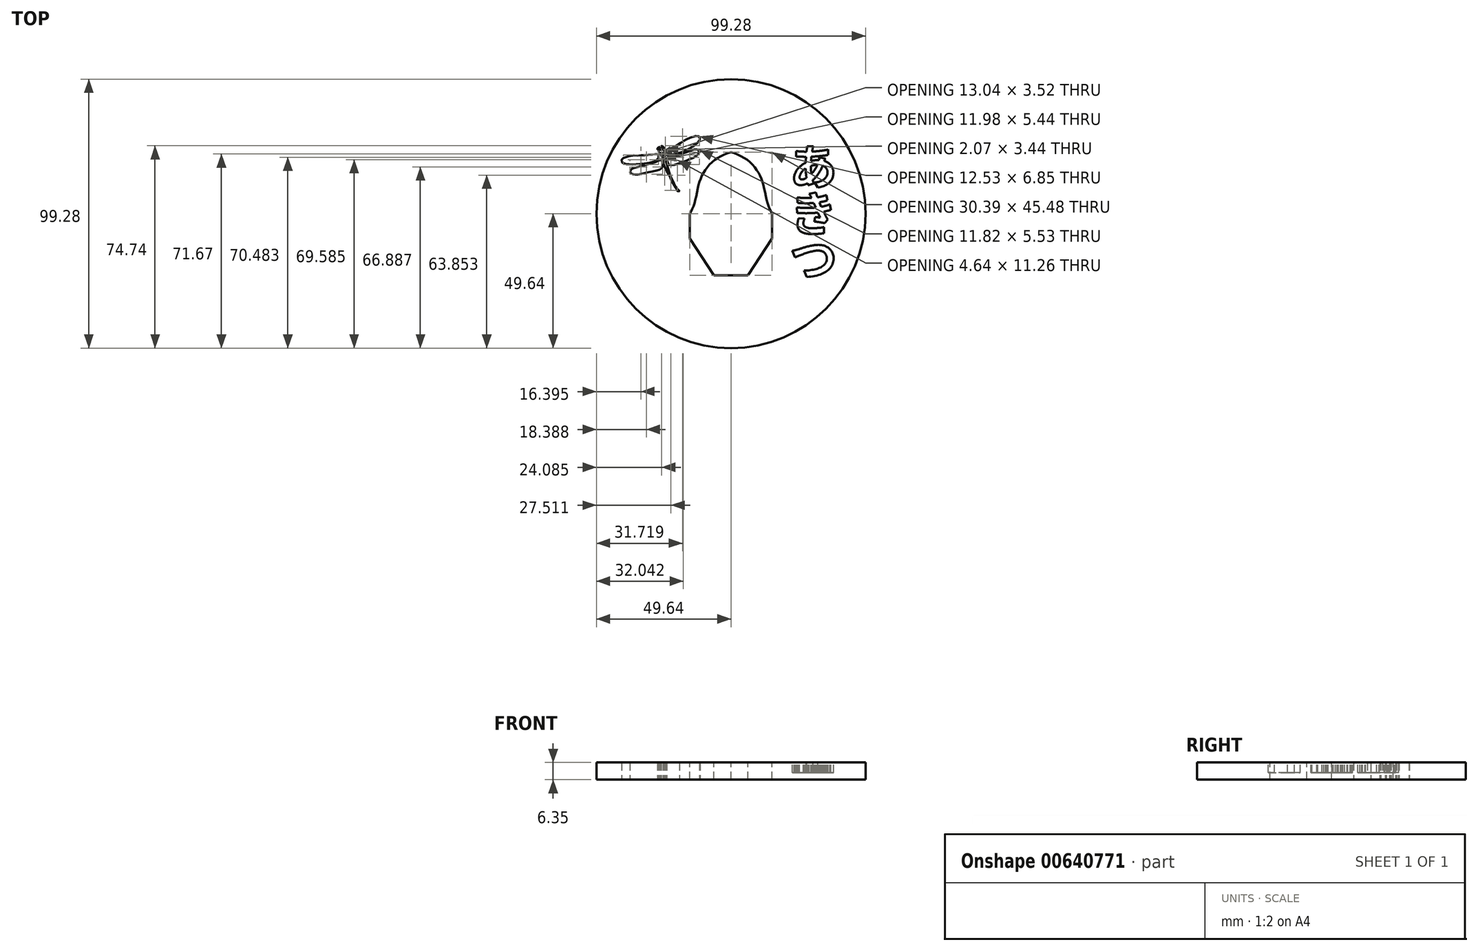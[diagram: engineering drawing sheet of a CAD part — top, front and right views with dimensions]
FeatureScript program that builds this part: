
annotation { "Feature Type Name" : "Feature", "Feature Type Description" : "" }
export const myFeature = defineFeature(function(context is Context, id is Id, definition is map)
    precondition{}
    {
        {
            var Q0;
            Q0=qCreatedBy(makeId("Top.planeOp"),FACE);
            var sketch = newSketch(context, id + "F0", { "sketchPlane" : qUnion([Q0])});
            skLineSegment(sketch, "E0.top", {"start": v(6.27, -22.74) * mm, "end": v(-6.27, -22.74) * mm});
            skLineSegment(sketch, "E0.left", {"start": v(15.2, 0) * mm, "end": v(15.2, -9.14) * mm});
            skLineSegment(sketch, "E0.right", {"start": v(-15.2, 0) * mm, "end": v(-15.2, -9.14) * mm});
            skPoint(sketch, "E0.middle", {"position": v(0, 0) * mm});
            skLineSegment(sketch, "E1", {"start": v(-15.2, -9.14) * mm, "end": v(-6.27, -22.74) * mm});
            skFitSpline(sketch, "E2", {"points": [v(0, 22.74) * mm, v(-5.84, 19.98) * mm, v(-9.88, 15.51) * mm, v(-12, 10.41) * mm, v(-13.5, 3.83) * mm, v(-15.2, 0) * mm], "startDerivative": vector(-29.13, -10.82) * mm, "endDerivative": vector(-10.85, -20.26) * mm});
            skFitSpline(sketch, "E3.MirrorCS", {"points": [v(0, 22.74) * mm, v(5.84, 19.98) * mm, v(9.88, 15.51) * mm, v(12, 10.41) * mm, v(13.5, 3.83) * mm, v(15.2, 0) * mm], "startDerivative": vector(29.13, -10.82) * mm, "endDerivative": vector(10.85, -20.26) * mm});
            skLineSegment(sketch, "E4.MirrorCS", {"start": v(15.2, -9.14) * mm, "end": v(6.27, -22.74) * mm});
            skPoint(sketch, "E5.orphan", {"position": v(-15.2, 22.74) * mm});
            skPoint(sketch, "E6.orphan", {"position": v(15.2, 22.74) * mm});
            skPoint(sketch, "E7.orphan", {"position": v(15.2, -22.74) * mm});
            skPoint(sketch, "E8.orphan", {"position": v(-15.2, -22.74) * mm});
            skCircle(sketch, "E9", {"center": v(0, 0) * mm, "radius": 49.64 * mm});
            skSolve(sketch);
        }
        {
            var Q0;
            Q0 = qSketchRegion(id + "F0", true);
            extrude(context, id + "F1", {"entities" : qUnion([Q0]), "oppositeDirection" : true, "depth" : 6.35 * mm, "offsetDistance" : 25.4 * mm});
        }
        {
            var Q0;
            Q0=qCreatedBy(makeId("Top.planeOp"),FACE);
            var sketch = newSketch(context, id + "F2", { "sketchPlane" : qUnion([Q0])});
            skEllipse(sketch, "E10", {"center": v(-25.17, 24.54) * mm, "majorRadius": 0.65 * mm, "minorRadius": 0.24 * mm, "majorAxis": v(0.78, -0.62)});
            skEllipse(sketch, "E11", {"center": v(-26.7, 24.17) * mm, "majorRadius": 0.6 * mm, "minorRadius": 0.27 * mm, "majorAxis": v(0.7, 0.72)});
            skFitSpline(sketch, "E12", {"points": [v(-24.63, 23.55) * mm, v(-24.92, 23.68) * mm, v(-25.48, 23.76) * mm, v(-26.25, 23.56) * mm, v(-26.58, 23.21) * mm, v(-26.45, 22.59) * mm, v(-26.17, 22.45) * mm, v(-25.86, 22.12) * mm, v(-25.2, 20.37) * mm, v(-24.92, 20.22) * mm, v(-24.5, 20.34) * mm, v(-24.4, 20.74) * mm, v(-24.47, 21.07) * mm, v(-24.94, 22.09) * mm, v(-24.7, 22.63) * mm, v(-24.61, 23.09) * mm, v(-24.63, 23.55) * mm]});
            skFitSpline(sketch, "E13", {"points": [v(-26.72, 21.52) * mm, v(-27.02, 21.84) * mm, v(-27.29, 22) * mm, v(-28.57, 21.85) * mm, v(-29.56, 21.78) * mm, v(-31.02, 21.63) * mm, v(-31.88, 21.6) * mm, v(-33, 21.52) * mm, v(-33.67, 21.56) * mm, v(-34.58, 21.5) * mm, v(-35.42, 21.52) * mm, v(-36.87, 21.36) * mm, v(-39.38, 20.7) * mm, v(-40.1, 20.26) * mm, v(-40.27, 20.02) * mm, v(-40.4, 19.74) * mm, v(-40.27, 19.1) * mm, v(-39.9, 18.74) * mm, v(-39.48, 18.6) * mm, v(-39.25, 18.5) * mm, v(-38.94, 18.35) * mm, v(-38.52, 18.3) * mm, v(-37.89, 18.24) * mm, v(-37.2, 18.2) * mm, v(-36.58, 18.16) * mm, v(-35.57, 18.17) * mm, v(-34.7, 18.24) * mm, v(-33.4, 18.37) * mm, v(-32.17, 18.51) * mm, v(-30.51, 18.74) * mm, v(-28.5, 19.27) * mm, v(-27.57, 19.76) * mm, v(-27.21, 20.09) * mm, v(-26.86, 20.35) * mm, v(-26.72, 20.61) * mm, v(-26.6, 20.87) * mm, v(-26.72, 21.52) * mm]});
            skFitSpline(sketch, "E14", {"points": [v(-25.84, 19.97) * mm, v(-26.57, 19.64) * mm, v(-27.78, 19.07) * mm, v(-32.7, 17.64) * mm, v(-35.23, 17.05) * mm, v(-36.57, 16.54) * mm, v(-36.96, 16.24) * mm, v(-37.1, 15.98) * mm, v(-37.24, 15.57) * mm, v(-37.05, 14.95) * mm, v(-36.8, 14.86) * mm, v(-36.57, 14.75) * mm, v(-36.18, 14.6) * mm, v(-35.83, 14.53) * mm, v(-34.87, 14.49) * mm, v(-33.96, 14.54) * mm, v(-30.95, 15.18) * mm, v(-27.58, 15.9) * mm, v(-26.54, 16.16) * mm, v(-25.83, 16.6) * mm, v(-25.49, 16.87) * mm, v(-25.35, 17.18) * mm, v(-25.21, 17.43) * mm, v(-25.18, 18.08) * mm, v(-25.44, 19.25) * mm, v(-25.84, 19.97) * mm]});
            skFitSpline(sketch, "E15", {"points": [v(-24.18, 22.87) * mm, v(-23.82, 23.22) * mm, v(-23.4, 23.47) * mm, v(-22.28, 24) * mm, v(-21.54, 24.43) * mm, v(-20.49, 24.9) * mm, v(-19.85, 25.34) * mm, v(-19.13, 25.7) * mm, v(-18.64, 26.1) * mm, v(-17.94, 26.46) * mm, v(-17.55, 26.8) * mm, v(-16.98, 27.15) * mm, v(-15.97, 27.59) * mm, v(-15.08, 28.02) * mm, v(-12.84, 28.73) * mm, v(-12.31, 28.6) * mm, v(-11.76, 28.55) * mm, v(-11.45, 27.76) * mm, v(-11.52, 27.18) * mm, v(-11.85, 26.9) * mm, v(-12, 26.65) * mm, v(-12.2, 26.37) * mm, v(-12.49, 26.06) * mm, v(-12.93, 25.77) * mm, v(-13.2, 25.43) * mm, v(-13.62, 25.12) * mm, v(-14.33, 24.73) * mm, v(-14.73, 24.42) * mm, v(-15.5, 24) * mm, v(-16.37, 23.55) * mm, v(-17.5, 23.06) * mm, v(-18.38, 22.7) * mm, v(-20.27, 22.13) * mm, v(-21.92, 21.6) * mm, v(-23.01, 21.4) * mm, v(-23.4, 21.52) * mm, v(-23.79, 21.61) * mm, v(-24.08, 21.94) * mm, v(-24.18, 22.87) * mm]});
            skFitSpline(sketch, "E16", {"points": [v(-23.5, 20.67) * mm, v(-22.94, 20.78) * mm, v(-18.44, 21.98) * mm, v(-16.44, 22.72) * mm, v(-13.83, 23.61) * mm, v(-12.95, 23.7) * mm, v(-12.5, 23.65) * mm, v(-12.05, 23.55) * mm, v(-11.68, 23.14) * mm, v(-11.72, 22.42) * mm, v(-11.92, 22.13) * mm, v(-12.24, 21.82) * mm, v(-12.87, 21.26) * mm, v(-13.3, 20.92) * mm, v(-14.5, 20.46) * mm, v(-15.73, 19.88) * mm, v(-17.89, 19.08) * mm, v(-19.64, 18.47) * mm, v(-21.74, 17.8) * mm, v(-22.11, 17.92) * mm, v(-22.6, 18.03) * mm, v(-22.9, 18.15) * mm, v(-23.2, 18.58) * mm, v(-23.74, 20.35) * mm, v(-23.5, 20.67) * mm]});
            skFitSpline(sketch, "E17", {"points": [v(-24.45, 19.84) * mm, v(-24.03, 19.43) * mm, v(-22.85, 15.27) * mm, v(-22.25, 13.71) * mm, v(-21.92, 12.85) * mm, v(-21.37, 11.91) * mm, v(-21.05, 11.05) * mm, v(-20.64, 10.25) * mm, v(-20.26, 9.82) * mm, v(-19.88, 9.22) * mm, v(-19.17, 8.62) * mm, v(-19.05, 8.23) * mm, v(-19.65, 8.24) * mm, v(-19.82, 8.66) * mm, v(-19.91, 8.89) * mm, v(-20.26, 9.32) * mm, v(-20.63, 9.9) * mm, v(-20.98, 10.49) * mm, v(-21.4, 11.3) * mm, v(-21.94, 12.36) * mm, v(-22.32, 13.18) * mm, v(-22.71, 14.07) * mm, v(-23.33, 14.97) * mm, v(-23.76, 15.93) * mm, v(-24.22, 16.78) * mm, v(-25.04, 19.43) * mm, v(-24.45, 19.84) * mm]});
            skLineSegment(sketch, "E18.0", {"start": v(-27.21, 18.44) * mm, "end": v(-24.45, 18.2) * mm, "construction": true});
            skLineSegment(sketch, "E19.0", {"start": v(-16.37, 21.9) * mm, "end": v(-11.68, 21.5) * mm, "construction": true});
            skLineSegment(sketch, "E20.0", {"start": v(-18.38, 21.05) * mm, "end": v(-11.92, 20.49) * mm, "construction": true});
            skLineSegment(sketch, "E21.0", {"start": v(-24.18, 21.23) * mm, "end": v(-12.24, 20.18) * mm, "construction": true});
            skLineSegment(sketch, "E22.0", {"start": v(-29.56, 20.14) * mm, "end": v(-14.5, 18.82) * mm, "construction": true});
            skLineSegment(sketch, "E23.0", {"start": v(-25.21, 15.8) * mm, "end": v(-25.04, 17.79) * mm, "construction": true});
            skLineSegment(sketch, "E24.0", {"start": v(-19.65, 6.6) * mm, "end": v(-18.38, 21.05) * mm, "construction": true});
            skLineSegment(sketch, "E25.0", {"start": v(-26.6, 19.23) * mm, "end": v(-26.45, 20.94) * mm, "construction": true});
            skLineSegment(sketch, "E26.0", {"start": v(-27.58, 14.25) * mm, "end": v(-27.21, 18.44) * mm, "construction": true});
            skLineSegment(sketch, "E27.0", {"start": v(-16.44, 21.08) * mm, "end": v(-16.37, 21.9) * mm, "construction": true});
            skLineSegment(sketch, "E28.0", {"start": v(-24.45, 18.2) * mm, "end": v(-24.18, 21.23) * mm, "construction": true});
            skSolve(sketch);
        }
        {
            var Q0;
            Q0 = qSketchRegion(id + "F2", true);
            extrude(context, id + "F3", {"entities" : qUnion([Q0]), "operationType" : NewBodyOperationType.REMOVE, "endBound" : BoundingType.THROUGH_ALL, "oppositeDirection" : true, "depth" : 25.4 * mm, "offsetDistance" : 25.4 * mm});
        }
        {
            var Q0;
            Q0=qCreatedBy(makeId("Top.planeOp"),FACE);
            var sketch = newSketch(context, id + "F4", { "sketchPlane" : qUnion([Q0])});
            skText(sketch, "E29", { "text": "あ", "fontName": "NotoSansCJKjp-Bold.otf"});
            skText(sketch, "E30", { "text": "き", "fontName": "NotoSansCJKjp-Bold.otf"});
            skText(sketch, "E31", { "text": "つ", "fontName": "NotoSansCJKjp-Bold.otf"});
            const initialGuessF4  = {"E29": [0.0216, 0.01067, 1, 0, 0.0127], "E30": [0.0216, -0.0066, 1, 0, 0.0127], "E31": [0.0216, -0.02337, 1, 0, 0.0127]};
            skSetInitialGuess(sketch, initialGuessF4);
            skSolve(sketch);
        }
        {
            var Q0;
            Q0 = qSketchRegion(id + "F4", true);
            extrude(context, id + "F5", {"entities" : qUnion([Q0]), "operationType" : NewBodyOperationType.REMOVE, "oppositeDirection" : true, "depth" : 3.8 * mm, "offsetDistance" : 25.4 * mm});
        }
    });
